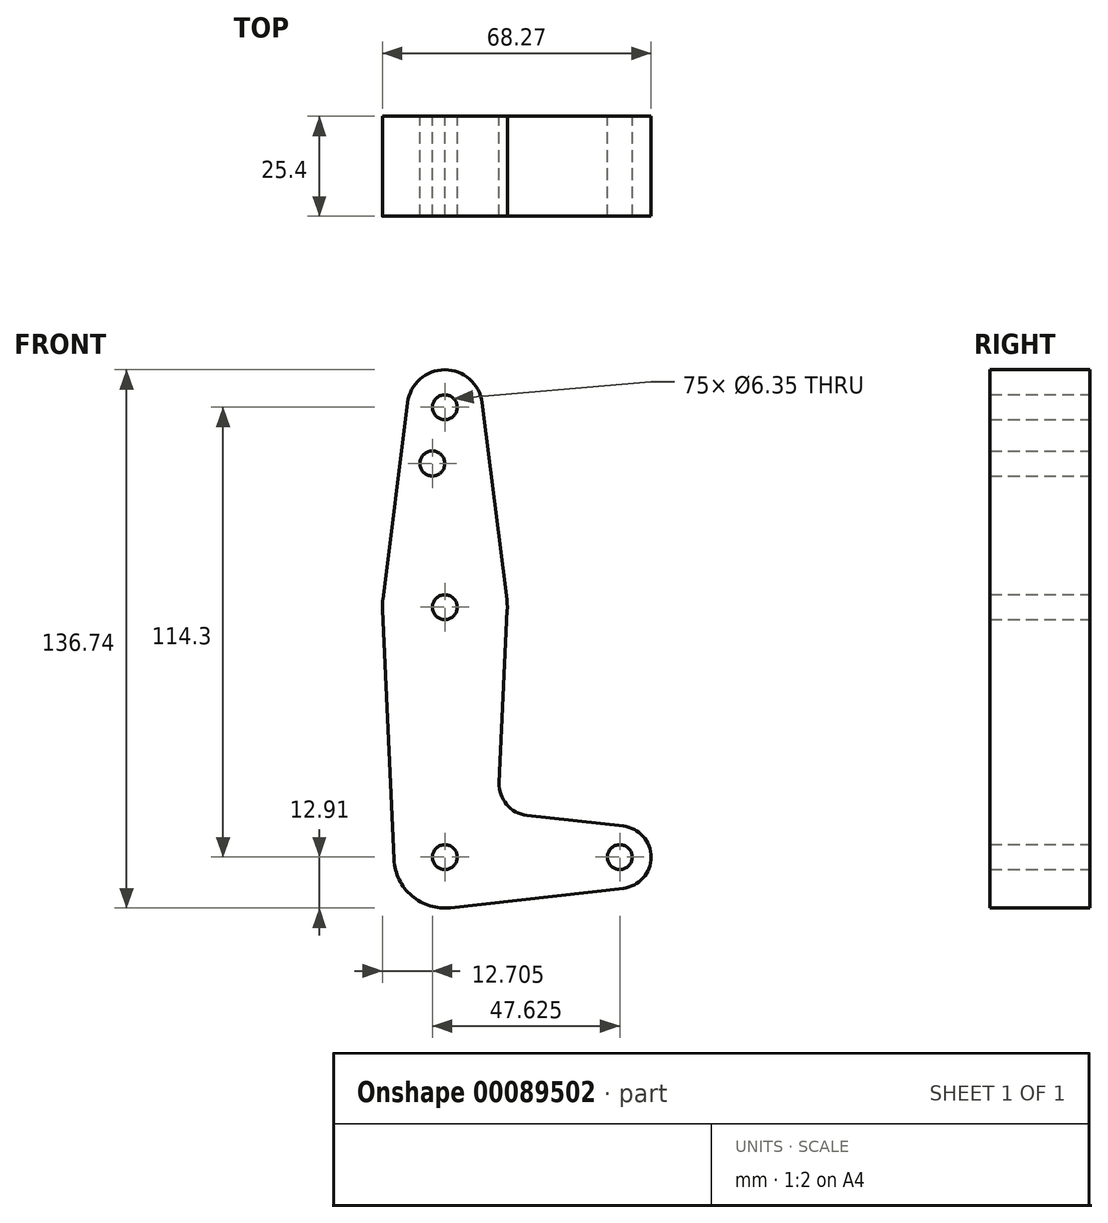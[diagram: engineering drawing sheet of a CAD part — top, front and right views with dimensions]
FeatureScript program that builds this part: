
annotation { "Feature Type Name" : "Feature", "Feature Type Description" : "" }
export const myFeature = defineFeature(function(context is Context, id is Id, definition is map)
    precondition{}
    {
        {
            var Q0;
            Q0=qCreatedBy(makeId("Front.planeOp"),FACE);
            var sketch = newSketch(context, id + "F0", { "sketchPlane" : qUnion([Q0])});
            skLineSegment(sketch, "E0", {"start": v(0, 0) * mm, "end": v(0, 114.3) * mm});
            skCircle(sketch, "E1", {"center": v(0, 63.5) * mm, "radius": 15.88 * mm});
            skCircle(sketch, "E2", {"center": v(0, 114.3) * mm, "radius": 9.53 * mm});
            skCircle(sketch, "E3", {"center": v(44.45, 0) * mm, "radius": 7.94 * mm});
            skLineSegment(sketch, "E4", {"start": v(9.45, 115.5) * mm, "end": v(15.75, 65.48) * mm});
            skLineSegment(sketch, "E5", {"start": v(-9.45, 115.5) * mm, "end": v(-15.98, 63.67) * mm});
            skCircle(sketch, "E6", {"center": v(0, 0) * mm, "radius": 12.91 * mm});
            skLineSegment(sketch, "E7", {"start": v(-15.86, 62.76) * mm, "end": v(-12.8, -2.78) * mm});
            skLineSegment(sketch, "E8", {"start": v(15.86, 62.76) * mm, "end": v(13.81, 18.92) * mm});
            skLineSegment(sketch, "E9", {"start": v(20.86, 10.65) * mm, "end": v(45.34, 7.89) * mm});
            skLineSegment(sketch, "E10", {"start": v(45.34, -7.89) * mm, "end": v(0, -13) * mm});
            skCircle(sketch, "E11", {"center": v(0, 114.3) * mm, "radius": 3.18 * mm});
            skCircle(sketch, "E12", {"center": v(-3.18, 100.03) * mm, "radius": 3.18 * mm});
            skCircle(sketch, "E13", {"center": v(0, 63.5) * mm, "radius": 3.18 * mm});
            skCircle(sketch, "E14", {"center": v(0, 0) * mm, "radius": 3.18 * mm});
            skCircle(sketch, "E15", {"center": v(44.45, 0) * mm, "radius": 3.18 * mm});
            skArc(sketch, "E16.filletArc", {"start": v(13.81, 18.92) * mm, "mid": v(15.7, 13.39) * mm, "end": v(20.86, 10.65) * mm});
            skSolve(sketch);
        }
        {
            var Q0;
            Q0 = qSketchRegion(id + "F0", true);
            extrude(context, id + "F1", {"entities" : qUnion([Q0]), "depth" : 25.4 * mm});
        }
    });
